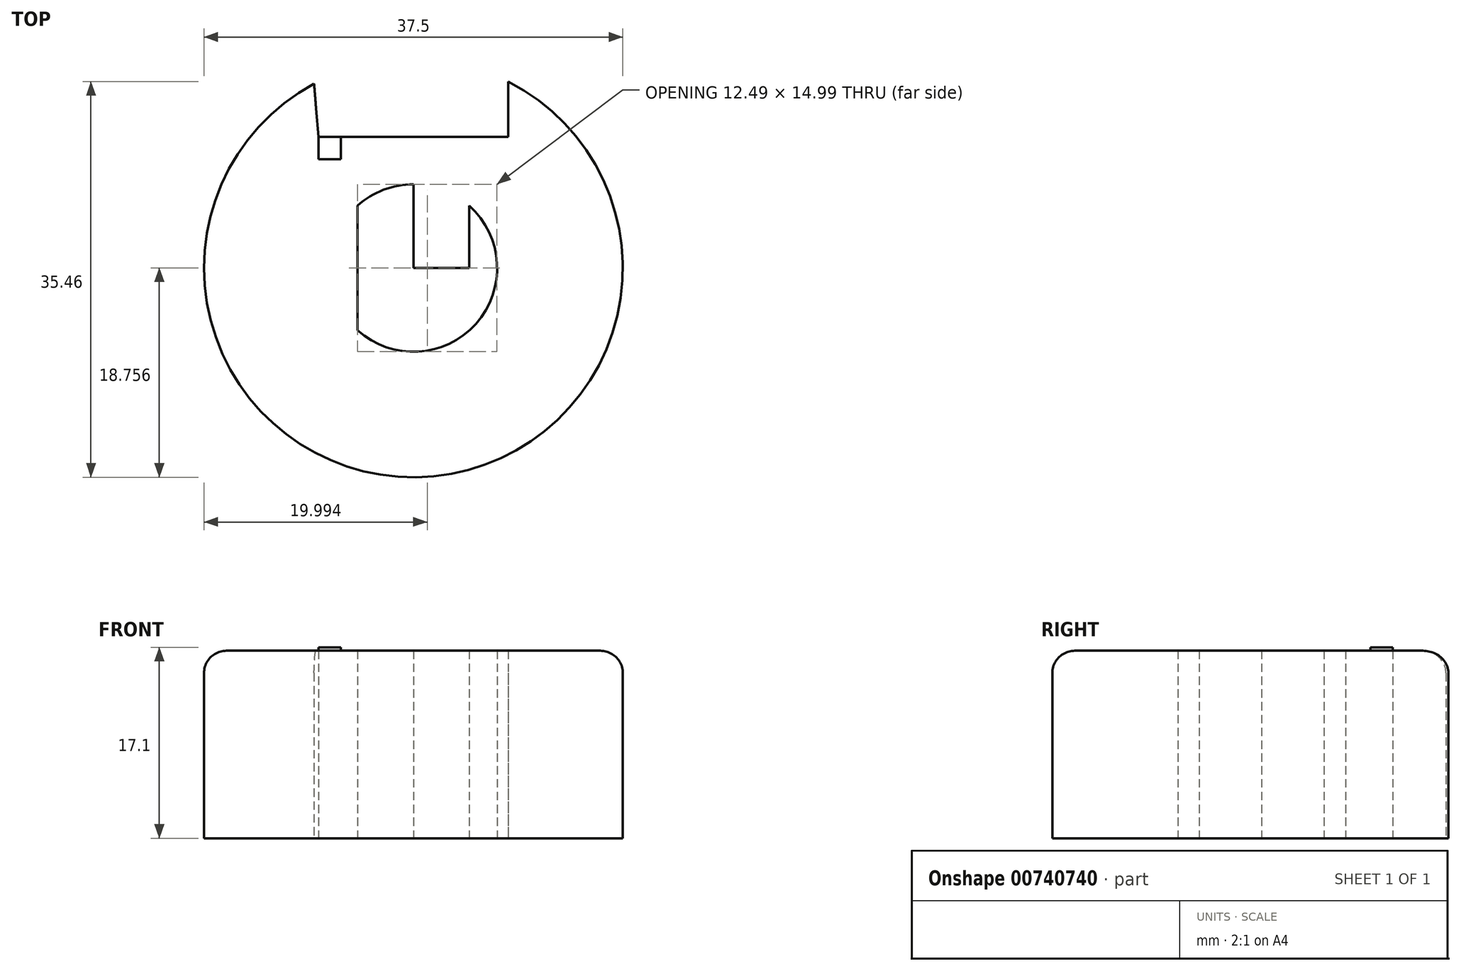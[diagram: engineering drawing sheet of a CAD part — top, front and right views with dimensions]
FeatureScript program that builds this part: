
annotation { "Feature Type Name" : "Feature", "Feature Type Description" : "" }
export const myFeature = defineFeature(function(context is Context, id is Id, definition is map)
    precondition{}
    {
        {
            var Q0;
            Q0=qCreatedBy(makeId("Top.planeOp"),FACE);
            var sketch = newSketch(context, id + "F0", { "sketchPlane" : qUnion([Q0])});
            skCircle(sketch, "E0", {"center": v(0, 0) * mm, "radius": 18.75 * mm});
            skCircle(sketch, "E1", {"center": v(0, 0) * mm, "radius": 7.5 * mm});
            skLineSegment(sketch, "E2", {"start": v(0, 0) * mm, "end": v(5, 0) * mm});
            skLineSegment(sketch, "E3", {"start": v(5, 0) * mm, "end": v(5, -5.6) * mm});
            skLineSegment(sketch, "E4", {"start": v(5, -5.6) * mm, "end": v(5, 5.6) * mm});
            skLineSegment(sketch, "E5", {"start": v(0, 0) * mm, "end": v(-5, 0) * mm});
            skLineSegment(sketch, "E6", {"start": v(-5, 5.6) * mm, "end": v(-5, -5.6) * mm});
            skLineSegment(sketch, "E7", {"start": v(0, 0) * mm, "end": v(0, 18.75) * mm});
            skLineSegment(sketch, "E8", {"start": v(0, 18.75) * mm, "end": v(0, 11.75) * mm});
            skLineSegment(sketch, "E9", {"start": v(8.5, 11.75) * mm, "end": v(0, 11.75) * mm});
            skLineSegment(sketch, "E10", {"start": v(8.5, 11.75) * mm, "end": v(8.5, 16.71) * mm});
            skLineSegment(sketch, "E11", {"start": v(0, 11.75) * mm, "end": v(-8.5, 11.75) * mm});
            skLineSegment(sketch, "E12", {"start": v(-8.5, 11.75) * mm, "end": v(-8.91, 16.71) * mm});
            skLineSegment(sketch, "E13", {"start": v(-8.5, 11.75) * mm, "end": v(-8.5, 9.75) * mm});
            skLineSegment(sketch, "E14", {"start": v(-8.5, 9.75) * mm, "end": v(-6.5, 9.75) * mm});
            skLineSegment(sketch, "E15", {"start": v(-6.5, 9.75) * mm, "end": v(-6.5, 11.75) * mm});
            skSolve(sketch);
        }
        {
            var Q0;
            Q0=makeQuery(id+"F0.imprint","IMPRINT",FACE,{"disambiguationData":[TD([[makeQuery(id+"F0.imprint","IMPRINT",EDGE,{"derivedFrom":sQuery(id+"F0.wireOp",EDGE,"E9")}),1.0]])]});
            var Q1;
            {var subQ0=sQuery(id+"F0.wireOp",EDGE,"E4");var subQ1=sQuery(id+"F0.wireOp",EDGE,"E1");var subQ2=makeQuery(id+"F0.imprint","INTERSECT",VERTEX,{"disambiguationData":[OD(0.0)],"derivedFrom":[subQ1,subQ0]});Q1=makeQuery(id+"F0.imprint","IMPRINT",FACE,{"disambiguationData":[TD([[makeQuery(id+"F0.imprint","IMPRINT",EDGE,{"disambiguationData":[TD([[subQ2,-1.0]])],"derivedFrom":subQ1}),1.0]])]});}
            var Q2;
            {var subQ0=sQuery(id+"F0.wireOp",EDGE,"E6");var subQ1=sQuery(id+"F0.wireOp",EDGE,"E1");var subQ2=makeQuery(id+"F0.imprint","INTERSECT",VERTEX,{"disambiguationData":[OD(0.0)],"derivedFrom":[subQ1,subQ0]});Q2=makeQuery(id+"F0.imprint","IMPRINT",FACE,{"disambiguationData":[TD([[makeQuery(id+"F0.imprint","IMPRINT",EDGE,{"disambiguationData":[TD([[subQ2,-1.0]])],"derivedFrom":subQ1}),1.0]])]});}
            extrude(context, id + "F1", {"entities" : qUnion([Q0, Q1, Q2]), "depth" : 16.8 * mm, "offsetDistance" : 25 * mm});
        }
        {
            var Q0;
            Q0=makeQuery(id+"F1.opExtrude","CAP_EDGE",EDGE,{"disambiguationData":[OSD([sQuery(id+"F0.wireOp",EDGE,"E0")])],"isStart":false});
            fillet(context, id + "F2", {"entities" : qUnion([Q0]), "radius" : 2 * mm, "tangentPropagation" : true, "allowEdgeOverflow" : false});
        }
        {
            var Q0;
            {var subQ0=sQuery(id+"F0.wireOp",EDGE,"E13");Q0=makeQuery(id+"F0.imprint","IMPRINT",FACE,{"disambiguationData":[TD([[makeQuery(id+"F0.imprint","IMPRINT",EDGE,{"derivedFrom":subQ0}),1.0]])]});}
            extrude(context, id + "F3", {"entities" : qUnion([Q0]), "operationType" : NewBodyOperationType.ADD, "depth" : 17.1 * mm, "offsetDistance" : 25 * mm, "hasSecondDirection" : true, "secondDirectionOppositeDirection" : true, "secondDirectionDepth" : 0 * mm});
        }
    });
